# Revit family: RN 82206 Optipress-Aquaplus-Valvola diritta
name_source: partatom
category: Rohrzubehör
units: mm (PartAtom-declared; Revit-internal decimal feet)

## family parameters
Arbeitsebenenbasiert = Nein
Beim Laden mit Abzugskörper schneiden = Nein
Bemaßung runder Anschluss = Durchmesser verwenden
Gemeinsam genutzt = Nein
Immer vertikal = Ja
Teiletyp = Ventil - Zerlegung in

## types (1)
- DN 20
    1.010.00.2 Number of the part of the guideline = 17
    1.010.00.3 Issue date (month) of the guideline = 201601
    1.010.00.4 Manufacturer name = R. Nussbaum AG
    1.010.00.5 Revision date of the file = 20190528
    1.100.00.3 Sort number for display sequence = 1
    1.100.00.4 Product designation = Rubinetti di chiusura
    1.800.00.3 BS number = 0010960000000000000000000000020070000000000000000100000000
    1.810.00.3 Manufacturer’s reference number = 82206.24
    1.810.00.4 DATANORM number = 82206.24
    1.810.00.5 StLB number = 623.444
    1.810.00.6 GTIN number = 7612945733009
    1.960/3L.00.8 Link (URL) = https://www.nussbaum.ch
    17.700.00.30 product description = 82206.24, Optipress-Aquaplus-Valvola diritta, con valvola di scarico, DN=20
    17.700.00.4 valve assembly type = 1
    17.700.00.5 nominal size DN = 20
    17.700.00.6 kvs-value [m3/h] = 5.86
    17.700.00.7 maximum operating temperature TB [°C] = 90
    17.700.00.8 maximum operating pressure(working pressure) ps [1.0 · 105 Pa] = 16
    CONNECTOR0_DIAMETER_dX_0r = 20 mm
    CONNECTOR0_dX_00 = 50 mm
    CONNECTOR0_dX_01 = 27 mm
    CONNECTOR0_ref_dX = 27 mm
    CONNECTOR1_DIAMETER_dX_0r = 20 mm
    CONNECTOR1_dX_00 = 27 mm
    CONNECTOR1_dX_01 = 50 mm
    CONNECTOR1_ref_dX = 27 mm
    Connector Visibility = Nein
    EnclosingSpace Visibility = Nein
    R. Nussbaum AG 82206.24 it Visibility = Ja

## geometry (parser evidence)
native form markers: Sweep x3
no freeform markers — native parametric forms only
